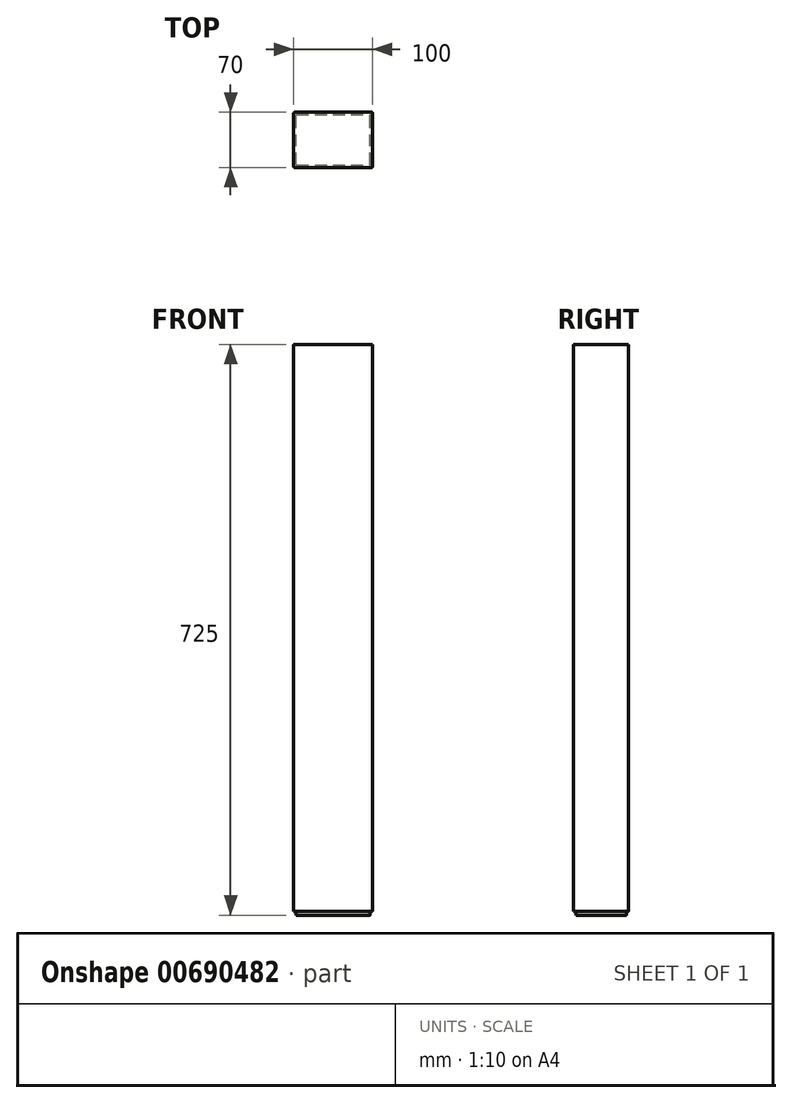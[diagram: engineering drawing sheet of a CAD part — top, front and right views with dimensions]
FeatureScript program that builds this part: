
annotation { "Feature Type Name" : "Feature", "Feature Type Description" : "" }
export const myFeature = defineFeature(function(context is Context, id is Id, definition is map)
    precondition{}
    {
        {
            var Q0;
            Q0=qCreatedBy(makeId("Top.planeOp"),FACE);
            var sketch = newSketch(context, id + "F0", { "sketchPlane" : qUnion([Q0])});
            skLineSegment(sketch, "E0.bottom", {"start": v(1, 0) * mm, "end": v(99, 0) * mm});
            skLineSegment(sketch, "E0.top", {"start": v(1, 70) * mm, "end": v(99, 70) * mm});
            skLineSegment(sketch, "E0.left", {"start": v(0, 1) * mm, "end": v(0, 69) * mm});
            skLineSegment(sketch, "E0.right", {"start": v(100, 1) * mm, "end": v(100, 69) * mm});
            skPoint(sketch, "E1.visualSharp", {"position": v(0, 70) * mm});
            skArc(sketch, "E1.filletArc", {"start": v(1, 70) * mm, "mid": v(0.3, 69.7) * mm, "end": v(0, 69) * mm});
            skPoint(sketch, "E2.visualSharp", {"position": v(100, 70) * mm});
            skArc(sketch, "E2.filletArc", {"start": v(100, 69) * mm, "mid": v(99.7, 69.7) * mm, "end": v(99, 70) * mm});
            skPoint(sketch, "E3.visualSharp", {"position": v(100, 0) * mm});
            skArc(sketch, "E3.filletArc", {"start": v(99, 0) * mm, "mid": v(99.7, 0.3) * mm, "end": v(100, 1) * mm});
            skPoint(sketch, "E4.visualSharp", {"position": v(0, 0) * mm});
            skArc(sketch, "E4.filletArc", {"start": v(0, 1) * mm, "mid": v(0.3, 0.3) * mm, "end": v(1, 0) * mm});
            skSolve(sketch);
        }
        {
            var Q0;
            Q0 = qSketchRegion(id + "F0", true);
            extrude(context, id + "F1", {"entities" : qUnion([Q0]), "oppositeDirection" : true, "depth" : 720 * mm, "offsetDistance" : 25 * mm});
        }
        {
            var Q0;
            Q0=makeQuery(id+"F1.opExtrude","CAP_FACE",FACE,{"disambiguationData":[OSD([sQuery(id+"F0.wireOp",EDGE,"E0.bottom"),sQuery(id+"F0.wireOp",EDGE,"E0.top"),sQuery(id+"F0.wireOp",EDGE,"E0.left"),sQuery(id+"F0.wireOp",EDGE,"E0.right"),sQuery(id+"F0.wireOp",EDGE,"E1.filletArc"),sQuery(id+"F0.wireOp",EDGE,"E2.filletArc"),sQuery(id+"F0.wireOp",EDGE,"E3.filletArc"),sQuery(id+"F0.wireOp",EDGE,"E4.filletArc")])],"isStart":true});
            var sketch = newSketch(context, id + "F2", { "sketchPlane" : qUnion([Q0])});
            skLineSegment(sketch, "E5.bottom", {"start": v(4, 3) * mm, "end": v(96, 3) * mm});
            skLineSegment(sketch, "E5.top", {"start": v(4, 67) * mm, "end": v(96, 67) * mm});
            skLineSegment(sketch, "E5.left", {"start": v(3, 4) * mm, "end": v(3, 66) * mm});
            skLineSegment(sketch, "E5.right", {"start": v(97, 4) * mm, "end": v(97, 66) * mm});
            skPoint(sketch, "E6.visualSharp", {"position": v(3, 67) * mm});
            skArc(sketch, "E6.filletArc", {"start": v(4, 67) * mm, "mid": v(3.3, 66.7) * mm, "end": v(3, 66) * mm});
            skPoint(sketch, "E7.visualSharp", {"position": v(97, 67) * mm});
            skArc(sketch, "E7.filletArc", {"start": v(97, 66) * mm, "mid": v(96.7, 66.7) * mm, "end": v(96, 67) * mm});
            skPoint(sketch, "E8.visualSharp", {"position": v(97, 3) * mm});
            skArc(sketch, "E8.filletArc", {"start": v(96, 3) * mm, "mid": v(96.7, 3.3) * mm, "end": v(97, 4) * mm});
            skPoint(sketch, "E9.visualSharp", {"position": v(3, 3) * mm});
            skArc(sketch, "E9.filletArc", {"start": v(3, 4) * mm, "mid": v(3.3, 3.3) * mm, "end": v(4, 3) * mm});
            skSolve(sketch);
        }
        {
            var Q0;
            Q0 = qSketchRegion(id + "F2", true);
            extrude(context, id + "F3", {"entities" : qUnion([Q0]), "operationType" : NewBodyOperationType.ADD, "oppositeDirection" : true, "depth" : 725 * mm, "offsetDistance" : 25 * mm});
        }
    });
